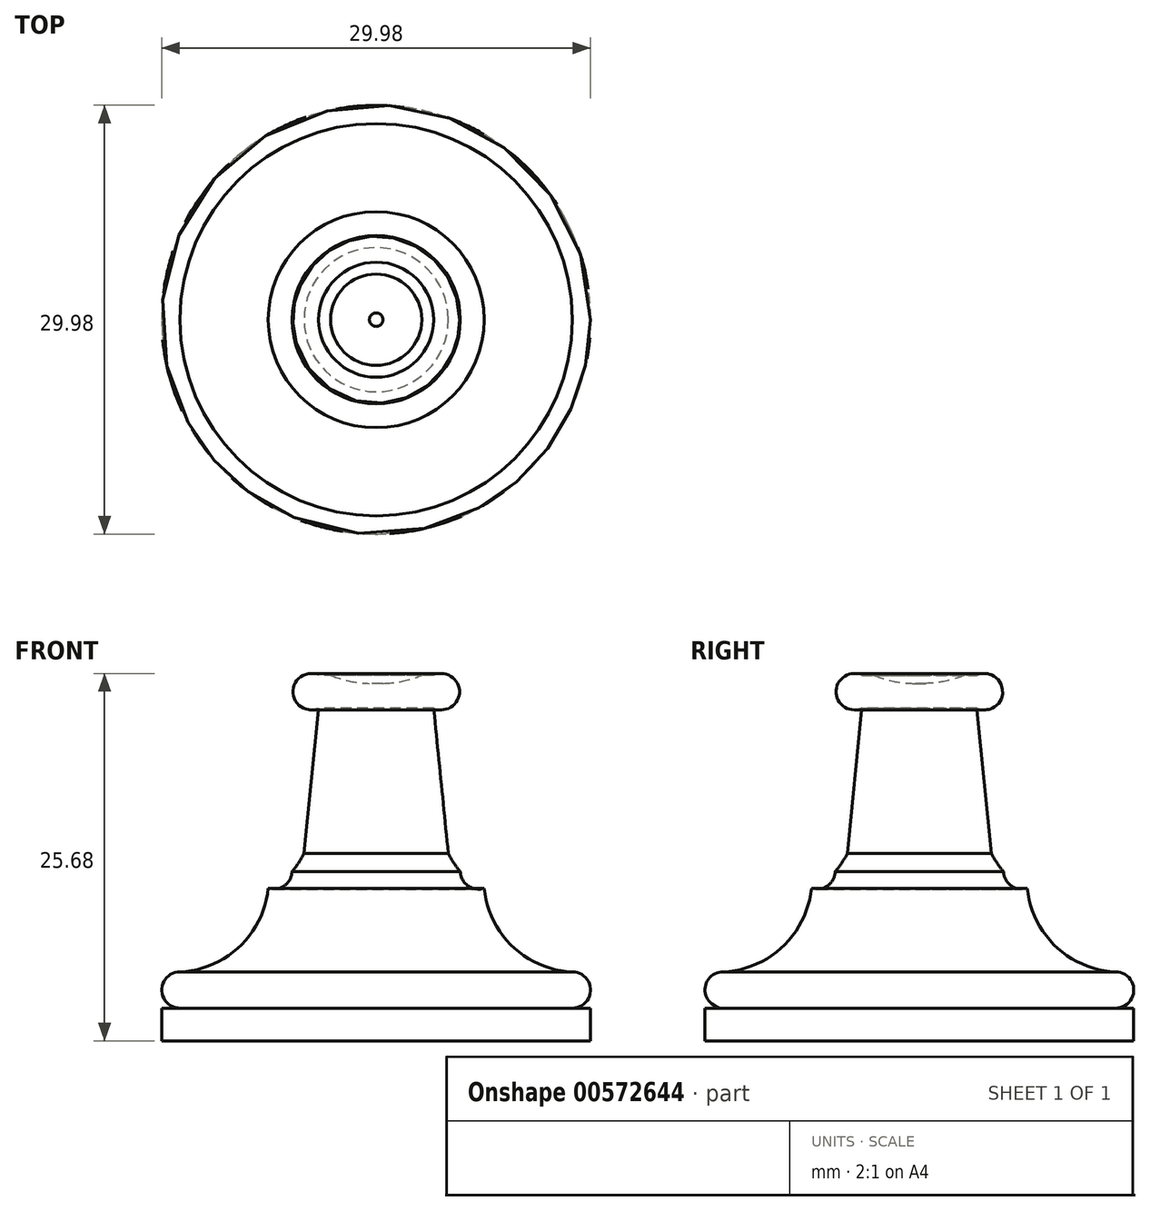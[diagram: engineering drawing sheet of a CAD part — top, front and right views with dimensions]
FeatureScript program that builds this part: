
annotation { "Feature Type Name" : "Feature", "Feature Type Description" : "" }
export const myFeature = defineFeature(function(context is Context, id is Id, definition is map)
    precondition{}
    {
        {
            var Q0;
            Q0=qCreatedBy(makeId("Front.planeOp"),FACE);
            var sketch = newSketch(context, id + "F0", { "sketchPlane" : qUnion([Q0])});
            skLineSegment(sketch, "E0", {"start": v(0, 0) * mm, "end": v(14.99, 0) * mm});
            skLineSegment(sketch, "E1", {"start": v(14.99, 0) * mm, "end": v(14.99, 2.29) * mm});
            skLineSegment(sketch, "E2", {"start": v(14.99, 2.29) * mm, "end": v(13.72, 2.29) * mm});
            skPoint(sketch, "E3.end.orphan", {"position": v(14.99, 7.03) * mm});
            skArc(sketch, "E4", {"start": v(13.72, 2.29) * mm, "mid": v(14.99, 3.56) * mm, "end": v(13.72, 4.83) * mm});
            skArc(sketch, "E5", {"start": v(7.55, 10.67) * mm, "mid": v(9.54, 6.6) * mm, "end": v(13.72, 4.83) * mm});
            skArc(sketch, "E6", {"start": v(5.88, 11.83) * mm, "mid": v(6.43, 10.83) * mm, "end": v(7.55, 10.67) * mm});
            skArc(sketch, "E7", {"start": v(5.04, 13.1) * mm, "mid": v(5.42, 12.44) * mm, "end": v(5.88, 11.83) * mm});
            skLineSegment(sketch, "E8", {"start": v(4.02, 23.26) * mm, "end": v(5.04, 13.1) * mm});
            skArc(sketch, "E9", {"start": v(4.02, 23.26) * mm, "mid": v(5.83, 24.4) * mm, "end": v(4.02, 25.56) * mm});
            skArc(sketch, "E10", {"start": v(3.2, 25.56) * mm, "mid": v(6.67, 28.44) * mm, "end": v(8.07, 32.73) * mm});
            skLineSegment(sketch, "E11", {"start": v(4.02, 25.56) * mm, "end": v(3.2, 25.56) * mm});
            skArc(sketch, "E12", {"start": v(3.2, 25.56) * mm, "mid": v(7.9, 34.44) * mm, "end": v(0, 40.66) * mm});
            skPoint(sketch, "E13.orphan", {"position": v(0, 41.14) * mm});
            skPoint(sketch, "E14.orphan", {"position": v(0, 24.89) * mm});
            skLineSegment(sketch, "E15", {"start": v(0, 41.14) * mm, "end": v(0, 0) * mm});
            skSolve(sketch);
        }
        {
            var Q0;
            Q0 = qSketchRegion(id + "F0", true);
            var Q1;
            Q1=sQuery(id+"F0.wireOp",EDGE,"E15");
            revolve(context, id + "F1", {"entities" : qUnion([Q0]), "axis" : qUnion([Q1]), "revolveType" : RevolveType.FULL});
        }
    });
